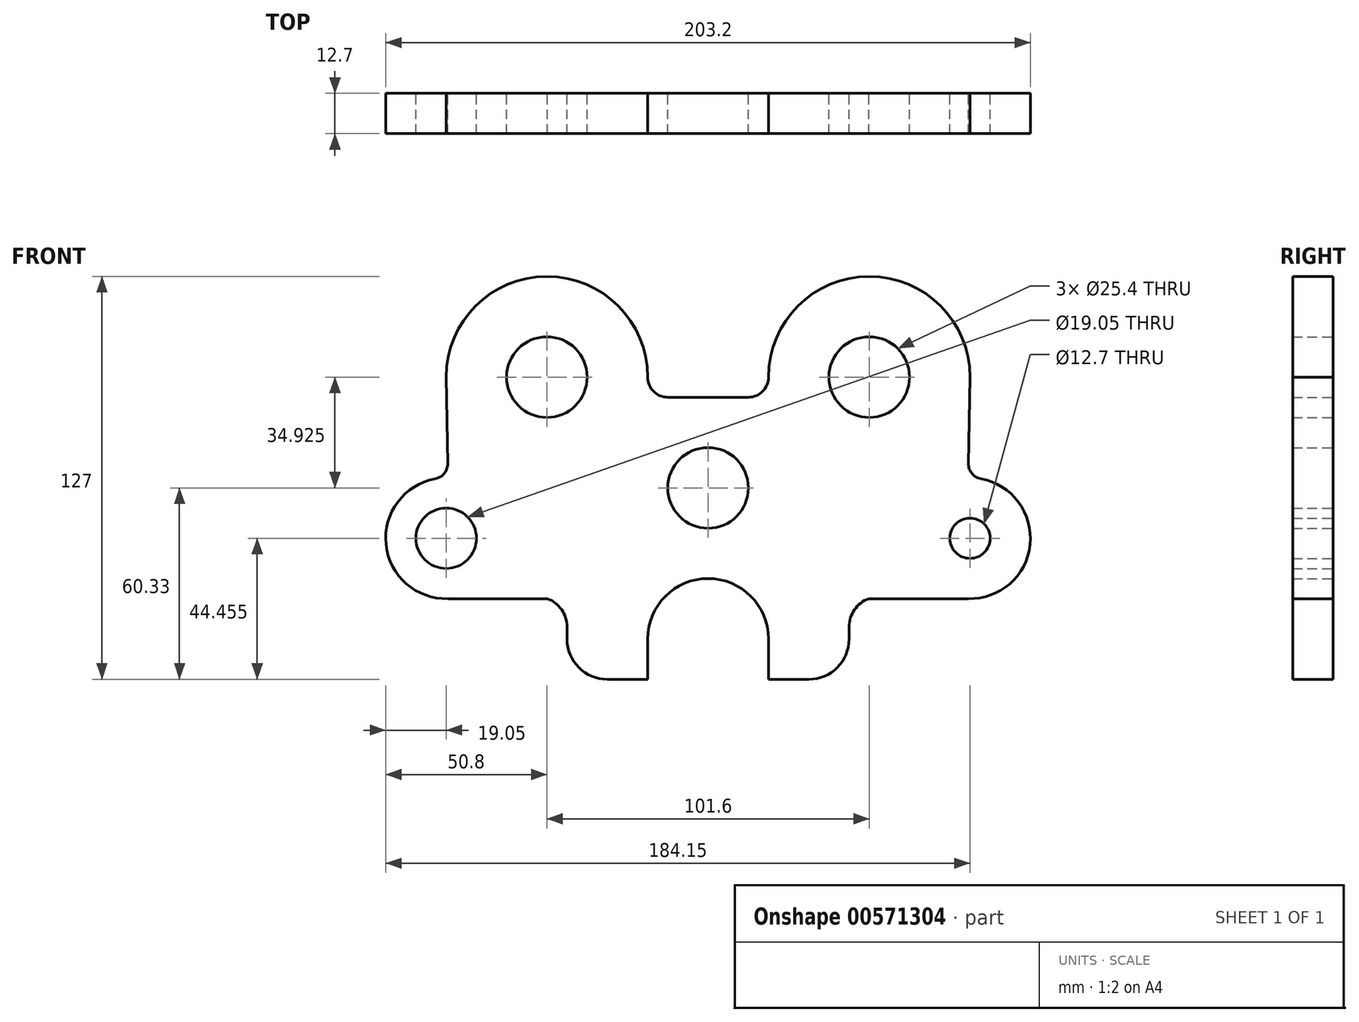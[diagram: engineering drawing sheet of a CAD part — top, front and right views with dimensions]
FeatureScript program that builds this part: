
annotation { "Feature Type Name" : "Feature", "Feature Type Description" : "" }
export const myFeature = defineFeature(function(context is Context, id is Id, definition is map)
    precondition{}
    {
        {
            var Q0;
            Q0=qCreatedBy(makeId("Front.planeOp"),FACE);
            var sketch = newSketch(context, id + "F0", { "sketchPlane" : qUnion([Q0])});
            skCircle(sketch, "E0", {"center": v(0, 0) * mm, "radius": 12.7 * mm});
            skCircle(sketch, "E1", {"center": v(50.8, 34.93) * mm, "radius": 12.7 * mm});
            skCircle(sketch, "E2", {"center": v(82.55, -15.87) * mm, "radius": 9.53 * mm});
            skLineSegment(sketch, "E3", {"start": v(0, 75.85) * mm, "end": v(0, -79.75) * mm, "construction": true});
            skCircle(sketch, "E4.MirrorC", {"center": v(-82.55, -15.87) * mm, "radius": 9.53 * mm});
            skArc(sketch, "E5", {"start": v(-19.05, -47.63) * mm, "mid": v(0, -28.58) * mm, "end": v(19.05, -47.63) * mm});
            skLineSegment(sketch, "E6", {"start": v(-19.05, -47.63) * mm, "end": v(0, -47.63) * mm, "construction": true});
            skLineSegment(sketch, "E7.MirrorCS", {"start": v(19.05, -47.63) * mm, "end": v(0, -47.63) * mm, "construction": true});
            skCircle(sketch, "E8.MirrorC", {"center": v(-50.8, 34.92) * mm, "radius": 12.7 * mm});
            skLineSegment(sketch, "E9", {"start": v(-19.05, -47.63) * mm, "end": v(-19.05, -60.33) * mm});
            skLineSegment(sketch, "E10", {"start": v(-19.05, -60.33) * mm, "end": v(-44.45, -60.33) * mm});
            skLineSegment(sketch, "E11", {"start": v(-44.45, -60.33) * mm, "end": v(-44.45, -43.85) * mm});
            skArc(sketch, "E12", {"start": v(-44.45, -43.85) * mm, "mid": v(-46.15, -38.4) * mm, "end": v(-50.66, -34.92) * mm});
            skLineSegment(sketch, "E13", {"start": v(-50.66, -34.92) * mm, "end": v(-82, -34.92) * mm});
            skArc(sketch, "E14", {"start": v(-82, -34.92) * mm, "mid": v(-101.6, -15.87) * mm, "end": v(-82, 3.17) * mm});
            skArc(sketch, "E15", {"start": v(-82.55, 34.93) * mm, "mid": v(-50.8, 66.67) * mm, "end": v(-19.05, 34.92) * mm});
            skArc(sketch, "E16.MirrorCS", {"start": v(82.55, 34.93) * mm, "mid": v(50.8, 66.68) * mm, "end": v(19.05, 34.93) * mm});
            skArc(sketch, "E17.MirrorCS", {"start": v(82, -34.92) * mm, "mid": v(101.6, -15.87) * mm, "end": v(82, 3.17) * mm});
            skLineSegment(sketch, "E18.MirrorCS", {"start": v(50.66, -34.92) * mm, "end": v(82, -34.92) * mm});
            skLineSegment(sketch, "E19.MirrorCS", {"start": v(44.45, -60.33) * mm, "end": v(44.45, -43.85) * mm});
            skArc(sketch, "E20.MirrorCS", {"start": v(44.45, -43.85) * mm, "mid": v(46.15, -38.4) * mm, "end": v(50.66, -34.92) * mm});
            skLineSegment(sketch, "E21.MirrorCS", {"start": v(19.05, -60.33) * mm, "end": v(44.45, -60.33) * mm});
            skLineSegment(sketch, "E22.MirrorCS", {"start": v(19.05, -47.63) * mm, "end": v(19.05, -60.33) * mm});
            skLineSegment(sketch, "E23", {"start": v(-82.55, 34.93) * mm, "end": v(-82, 3.17) * mm});
            skLineSegment(sketch, "E24", {"start": v(82.55, 34.93) * mm, "end": v(82, 3.17) * mm});
            skLineSegment(sketch, "E25", {"start": v(-19.05, 34.92) * mm, "end": v(-19.05, 28.57) * mm});
            skLineSegment(sketch, "E26.MirrorCS", {"start": v(19.05, 34.92) * mm, "end": v(19.05, 28.57) * mm});
            skLineSegment(sketch, "E27", {"start": v(-19.05, 28.57) * mm, "end": v(19.05, 28.57) * mm});
            skCircle(sketch, "E28", {"center": v(-82.55, -15.87) * mm, "radius": 6.35 * mm});
            skCircle(sketch, "E29.MirrorC", {"center": v(82.55, -15.87) * mm, "radius": 6.35 * mm});
            skSolve(sketch);
        }
        {
            var Q0;
            Q0=qSketchRegion(id+"F0",true);
            var Q1;
            Q1=makeQuery(id+"F0.imprint","IMPRINT",FACE,{"disambiguationData":[TD([[makeQuery(id+"F0.imprint","IMPRINT",EDGE,{"derivedFrom":sQuery(id+"F0.wireOp",EDGE,"E2")}),1.0]])]});
            var Q2;
            Q2=makeQuery(id+"F0.imprint","IMPRINT",FACE,{"disambiguationData":[TD([[makeQuery(id+"F0.imprint","IMPRINT",EDGE,{"derivedFrom":sQuery(id+"F0.wireOp",EDGE,"E4.MirrorC")}),-1.0]])]});
            extrude(context, id + "F1", {"entities" : qUnion([Q0, Q1, Q2]), "endBound" : BoundingType.SYMMETRIC, "depth" : 12.7 * mm, "offsetDistance" : 25.4 * mm});
        }
        {
            var Q0;
            Q0=makeQuery(id+"F1.opExtrude","SWEPT_EDGE",EDGE,{"disambiguationData":[OSD([sQuery(id+"F0.wireOp",EDGE,"E10"),sQuery(id+"F0.wireOp",EDGE,"E11")])]});
            var Q1;
            Q1=makeQuery(id+"F1.opExtrude","SWEPT_EDGE",EDGE,{"disambiguationData":[OSD([sQuery(id+"F0.wireOp",EDGE,"E19.MirrorCS"),sQuery(id+"F0.wireOp",EDGE,"E21.MirrorCS")])]});
            fillet(context, id + "F2", {"entities" : qUnion([Q0, Q1]), "radius" : 12.7 * mm, "tangentPropagation" : true, "allowEdgeOverflow" : false});
        }
        {
            var Q0;
            Q0=makeQuery(id+"F1.opExtrude","SWEPT_EDGE",EDGE,{"disambiguationData":[OSD([sQuery(id+"F0.wireOp",EDGE,"E14"),sQuery(id+"F0.wireOp",EDGE,"E23")])]});
            var Q1;
            Q1=makeQuery(id+"F1.opExtrude","SWEPT_EDGE",EDGE,{"disambiguationData":[OSD([sQuery(id+"F0.wireOp",EDGE,"E17.MirrorCS"),sQuery(id+"F0.wireOp",EDGE,"E24")])]});
            fillet(context, id + "F3", {"entities" : qUnion([Q0, Q1]), "radius" : 4.76 * mm, "tangentPropagation" : true, "allowEdgeOverflow" : false});
        }
        {
            var Q0;
            Q0=makeQuery(id+"F1.opExtrude","SWEPT_EDGE",EDGE,{"disambiguationData":[OSD([sQuery(id+"F0.wireOp",EDGE,"E25"),sQuery(id+"F0.wireOp",EDGE,"E27")])]});
            var Q1;
            Q1=makeQuery(id+"F1.opExtrude","SWEPT_EDGE",EDGE,{"disambiguationData":[OSD([sQuery(id+"F0.wireOp",EDGE,"E26.MirrorCS"),sQuery(id+"F0.wireOp",EDGE,"E27")])]});
            fillet(context, id + "F4", {"entities" : qUnion([Q0, Q1]), "radius" : 6.35 * mm, "tangentPropagation" : true, "allowEdgeOverflow" : false});
        }
    });
